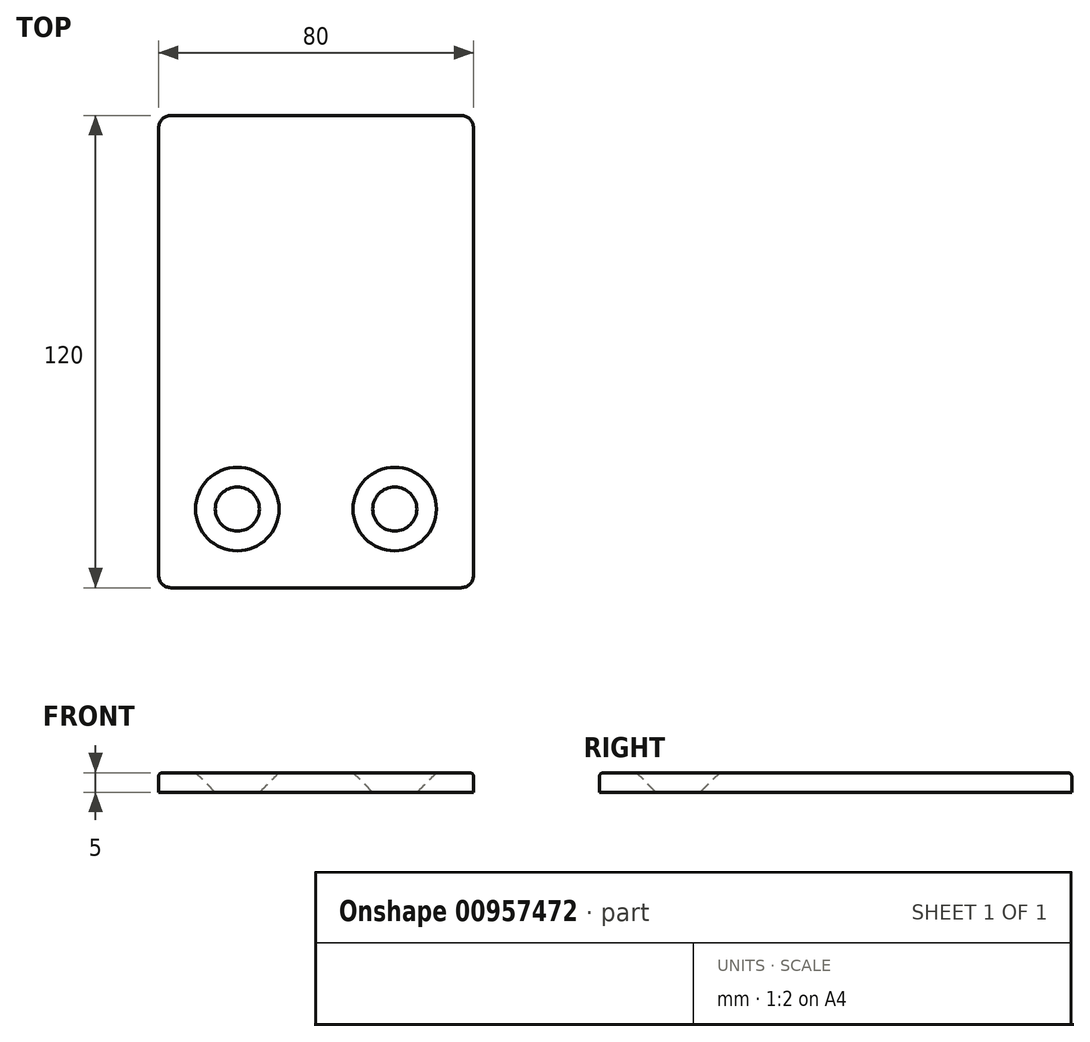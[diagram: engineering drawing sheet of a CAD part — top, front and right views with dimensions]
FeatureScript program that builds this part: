
annotation { "Feature Type Name" : "Feature", "Feature Type Description" : "" }
export const myFeature = defineFeature(function(context is Context, id is Id, definition is map)
    precondition{}
    {
        {
            var Q0;
            Q0=qCreatedBy(makeId("Top.planeOp"),FACE);
            var sketch = newSketch(context, id + "F0", { "sketchPlane" : qUnion([Q0])});
            skLineSegment(sketch, "E0.bottom", {"start": v(-36.83, -60) * mm, "end": v(36.83, -60) * mm});
            skLineSegment(sketch, "E0.top", {"start": v(-36.83, 60) * mm, "end": v(36.83, 60) * mm});
            skLineSegment(sketch, "E0.left", {"start": v(-40, -56.83) * mm, "end": v(-40, 56.83) * mm});
            skLineSegment(sketch, "E0.right", {"start": v(40, -56.83) * mm, "end": v(40, 56.83) * mm});
            skLineSegment(sketch, "E1", {"start": v(40, 60) * mm, "end": v(-40, -60) * mm, "construction": true});
            skLineSegment(sketch, "E2", {"start": v(-40, 60) * mm, "end": v(40, -60) * mm, "construction": true});
            skCircle(sketch, "E3", {"center": v(-20, -40.01) * mm, "radius": 5 * mm});
            skCircle(sketch, "E4", {"center": v(20, -40.01) * mm, "radius": 5 * mm});
            skPoint(sketch, "E5.visualSharp", {"position": v(-40, -60) * mm});
            skArc(sketch, "E5.filletArc", {"start": v(-40, -56.83) * mm, "mid": v(-39.07, -59.07) * mm, "end": v(-36.83, -60) * mm});
            skPoint(sketch, "E6.visualSharp", {"position": v(40, -60) * mm});
            skArc(sketch, "E6.filletArc", {"start": v(36.83, -60) * mm, "mid": v(39.07, -59.07) * mm, "end": v(40, -56.83) * mm});
            skPoint(sketch, "E7.visualSharp", {"position": v(-40, 60) * mm});
            skArc(sketch, "E7.filletArc", {"start": v(-36.83, 60) * mm, "mid": v(-39.07, 59.07) * mm, "end": v(-40, 56.83) * mm});
            skPoint(sketch, "E8.visualSharp", {"position": v(40, 60) * mm});
            skArc(sketch, "E8.filletArc", {"start": v(40, 56.83) * mm, "mid": v(39.07, 59.07) * mm, "end": v(36.83, 60) * mm});
            skSolve(sketch);
        }
        {
            var Q0;
            Q0 = qSketchRegion(id + "F0", true);
            extrude(context, id + "F1", {"entities" : qUnion([Q0]), "depth" : 5 * mm, "offsetDistance" : 25 * mm});
        }
        {
            var Q0;
            Q0=makeQuery(id+"F1.opExtrude","CAP_EDGE",EDGE,{"disambiguationData":[OSD([sQuery(id+"F0.wireOp",EDGE,"E0.left")])],"isStart":false});
            fillet(context, id + "F2", {"entities" : qUnion([Q0]), "radius" : 1 * mm, "tangentPropagation" : true, "allowEdgeOverflow" : false});
        }
        {
            var Q0;
            Q0=makeQuery(id+"F1.opExtrude","CAP_EDGE",EDGE,{"disambiguationData":[OSD([sQuery(id+"F0.wireOp",EDGE,"E3")])],"isStart":false});
            var Q1;
            Q1=makeQuery(id+"F1.opExtrude","CAP_EDGE",EDGE,{"disambiguationData":[OSD([sQuery(id+"F0.wireOp",EDGE,"E4")])],"isStart":false});
            chamfer(context, id + "F3", {"entities" : qUnion([Q0, Q1]), "chamferType" : ChamferType.OFFSET_ANGLE, "width" : 5.6 * mm, "oppositeDirection" : false, "angle" : 45 * degree, "tangentPropagation" : true});
        }
    });
